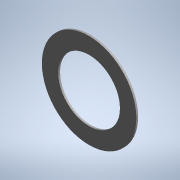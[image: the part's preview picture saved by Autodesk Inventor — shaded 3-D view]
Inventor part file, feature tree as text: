
AUTODESK INVENTOR PART (.ipt)
format: ipt  version: 2020 (Build 240168000, 168)  size: 82,432 bytes
history: native  units: mm (DEFAULTED — no unit token found)
features: other x6, extrude x1, sketch x1
ambient origin geometry x1: 原点
bodies: 实体1 (feature_tree)
feature tree (8):
  extrude  "拉伸1"  Depth=0.5mm
  other  "YZ 平面"
  other  "XZ 平面"
  other  "XY 平面"
  other  "X 轴"
  other  "Y 轴"
  other  "Z 轴"
  sketch  "草图1"  dims[d0=26.0mm d1=17.0mm d2=0.5mm d3=0.0mm d4=5.0mm d5=0.872665mm]
